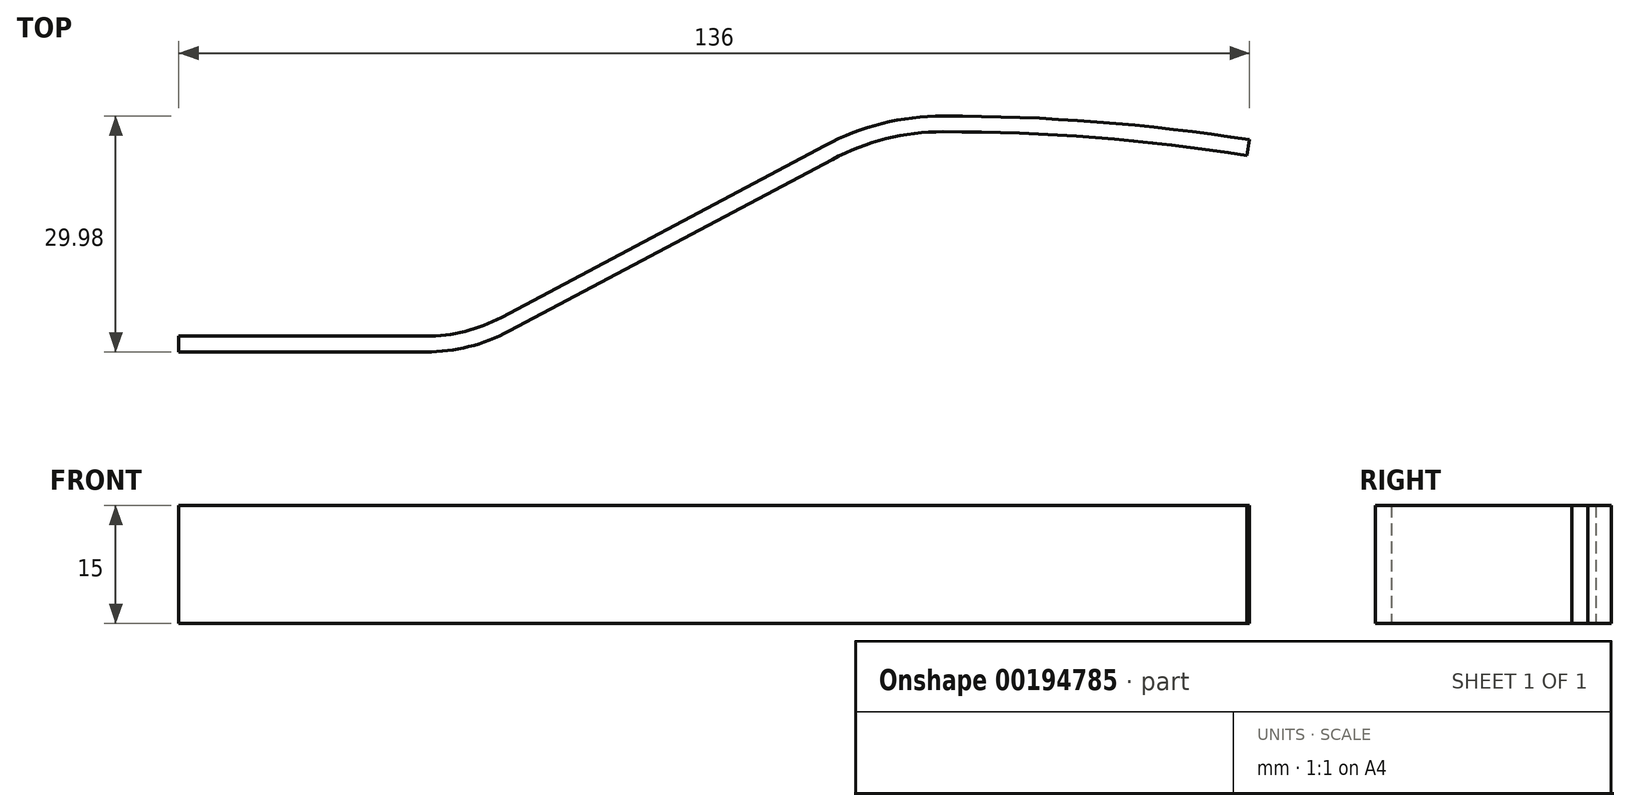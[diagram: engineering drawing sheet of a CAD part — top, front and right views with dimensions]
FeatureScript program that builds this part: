
annotation { "Feature Type Name" : "Feature", "Feature Type Description" : "" }
export const myFeature = defineFeature(function(context is Context, id is Id, definition is map)
    precondition{}
    {
        {
            var Q0;
            Q0=qCreatedBy(makeId("Top.planeOp"),FACE);
            var sketch = newSketch(context, id + "F0", { "sketchPlane" : qUnion([Q0])});
            skLineSegment(sketch, "E0", {"start": v(0, 0) * mm, "end": v(31.4, 0) * mm});
            skLineSegment(sketch, "E1", {"start": v(41.95, 2.63) * mm, "end": v(83.01, 24.46) * mm});
            skPoint(sketch, "E2.visualSharp", {"position": v(37, 0) * mm});
            skArc(sketch, "E2.filletArc", {"start": v(31.4, 0) * mm, "mid": v(36.83, 0.67) * mm, "end": v(41.95, 2.63) * mm});
            skPoint(sketch, "E3.visualSharp", {"position": v(92.63, 29.58) * mm});
            skArc(sketch, "E3.filletArc", {"start": v(97.1, 27.98) * mm, "mid": v(89.84, 27.08) * mm, "end": v(83.01, 24.46) * mm});
            skArc(sketch, "E4", {"start": v(97.1, 27.98) * mm, "mid": v(116.45, 27.23) * mm, "end": v(135.7, 24.98) * mm});
            skArc(sketch, "E5.0", {"start": v(97.1, 29.98) * mm, "mid": v(116.6, 29.22) * mm, "end": v(136, 26.95) * mm});
            skLineSegment(sketch, "E5.1", {"start": v(0, 2) * mm, "end": v(31.4, 2) * mm});
            skArc(sketch, "E5.2", {"start": v(31.4, 2) * mm, "mid": v(36.35, 2.6) * mm, "end": v(41.01, 4.4) * mm});
            skLineSegment(sketch, "E5.3", {"start": v(41.01, 4.4) * mm, "end": v(82.07, 26.23) * mm});
            skArc(sketch, "E5.4", {"start": v(97.1, 29.98) * mm, "mid": v(89.35, 29.03) * mm, "end": v(82.07, 26.23) * mm});
            skLineSegment(sketch, "E6", {"start": v(0, 0) * mm, "end": v(0, 2) * mm});
            skLineSegment(sketch, "E7", {"start": v(135.7, 24.98) * mm, "end": v(136, 26.95) * mm});
            skSolve(sketch);
        }
        {
            var Q0;
            Q0 = qSketchRegion(id + "F0", true);
            extrude(context, id + "F1", {"entities" : qUnion([Q0]), "depth" : 15 * mm});
        }
    });
